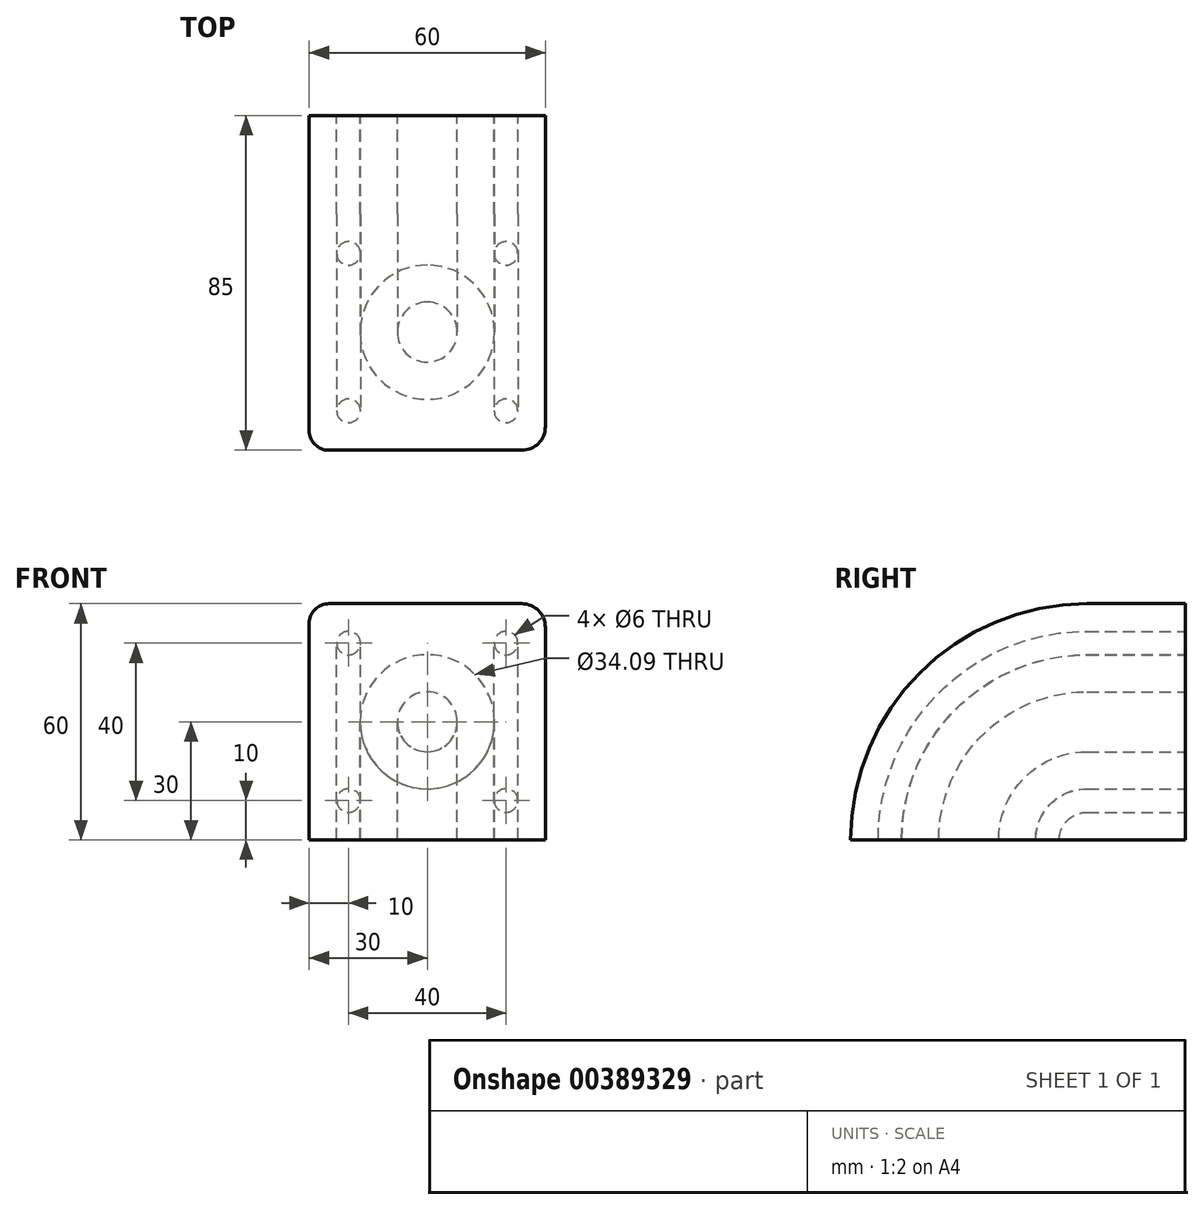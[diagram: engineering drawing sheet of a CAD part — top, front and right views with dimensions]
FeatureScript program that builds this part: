
annotation { "Feature Type Name" : "Feature", "Feature Type Description" : "" }
export const myFeature = defineFeature(function(context is Context, id is Id, definition is map)
    precondition{}
    {
        {
            var Q0;
            Q0=qCreatedBy(makeId("Front.planeOp"),FACE);
            var sketch = newSketch(context, id + "F0", { "sketchPlane" : qUnion([Q0])});
            skLineSegment(sketch, "E0.bottom", {"start": v(-30, 30) * mm, "end": v(24, 30) * mm});
            skLineSegment(sketch, "E0.top", {"start": v(-30, -30) * mm, "end": v(30, -30) * mm});
            skLineSegment(sketch, "E0.left", {"start": v(-30, 30) * mm, "end": v(-30, -30) * mm});
            skLineSegment(sketch, "E0.right", {"start": v(30, 24) * mm, "end": v(30, -30) * mm});
            skCircle(sketch, "E1", {"center": v(-20, 20) * mm, "radius": 3 * mm});
            skCircle(sketch, "E2", {"center": v(20, 20) * mm, "radius": 3 * mm});
            skCircle(sketch, "E3", {"center": v(20, -20) * mm, "radius": 3 * mm});
            skCircle(sketch, "E4", {"center": v(-20, -20) * mm, "radius": 3 * mm});
            skLineSegment(sketch, "E5.bottom", {"start": v(-20, 20) * mm, "end": v(20, 20) * mm, "construction": true});
            skLineSegment(sketch, "E5.top", {"start": v(-20, -20) * mm, "end": v(20, -20) * mm, "construction": true});
            skLineSegment(sketch, "E5.left", {"start": v(-20, 20) * mm, "end": v(-20, -20) * mm, "construction": true});
            skLineSegment(sketch, "E5.right", {"start": v(20, 20) * mm, "end": v(20, -20) * mm, "construction": true});
            skLineSegment(sketch, "E6", {"start": v(-20, 20) * mm, "end": v(20, -20) * mm, "construction": true});
            skLineSegment(sketch, "E7", {"start": v(30, 30) * mm, "end": v(-30, -30) * mm, "construction": true});
            skPoint(sketch, "E8.visualSharp", {"position": v(-30, 30) * mm});
            skPoint(sketch, "E9.visualSharp", {"position": v(30, 30) * mm});
            skArc(sketch, "E9.filletArc", {"start": v(30, 24) * mm, "mid": v(28.24, 28.24) * mm, "end": v(24, 30) * mm});
            skCircle(sketch, "E10", {"center": v(0, 0) * mm, "radius": 17.05 * mm});
            skCircle(sketch, "E11", {"center": v(0, 0) * mm, "radius": 7.61 * mm});
            skSolve(sketch);
        }
        {
            var Q0;
            Q0 = qSketchRegion(id + "F0", true);
            var Q1;
            Q1=makeQuery(id+"F0.imprint","IMPRINT",FACE,{"disambiguationData":[TD([[makeQuery(id+"F0.imprint","IMPRINT",EDGE,{"derivedFrom":sQuery(id+"F0.wireOp",EDGE,"E11")}),1.0]])]});
            extrude(context, id + "F1", {"entities" : qUnion([Q0, Q1]), "depth" : 25 * mm, "offsetDistance" : 25 * mm});
        }
        {
            var Q0;
            Q0=makeQuery(id+"F1.opExtrude","CAP_FACE",FACE,{"disambiguationData":[OSD([sQuery(id+"F0.wireOp",EDGE,"E0.bottom"),sQuery(id+"F0.wireOp",EDGE,"E0.top"),sQuery(id+"F0.wireOp",EDGE,"E0.left"),sQuery(id+"F0.wireOp",EDGE,"E0.right"),sQuery(id+"F0.wireOp",EDGE,"E1"),sQuery(id+"F0.wireOp",EDGE,"E2"),sQuery(id+"F0.wireOp",EDGE,"E3"),sQuery(id+"F0.wireOp",EDGE,"E4")])],"isStart":false});
            var Q1;
            Q1=makeQuery(id+"F1.opExtrude","CAP_FACE",FACE,{"disambiguationData":[OSD([sQuery(id+"F0.wireOp",EDGE,"E11")])],"isStart":false});
            var Q2;
            Q2=makeQuery(id+"F1.opExtrude","CAP_EDGE",EDGE,{"disambiguationData":[OSD([sQuery(id+"F0.wireOp",EDGE,"E0.top")])],"isStart":false});
            revolve(context, id + "F2", {"operationType" : NewBodyOperationType.ADD, "surfaceOperationType" : NewSurfaceOperationType.NEW, "entities" : qUnion([Q0, Q1]), "axis" : qUnion([Q2]), "revolveType" : RevolveType.ONE_DIRECTION, "angle" : 90 * degree});
        }
        {
            var Q0;
            Q0=makeQuery(id+"F2.opRevolve","SWEPT_EDGE",EDGE,{"disambiguationData":[OSD([sQuery(id+"F0.wireOp",EDGE,"E0.bottom"),sQuery(id+"F0.wireOp",EDGE,"E0.left")])]});
            var Q1;
            Q1=makeQuery(id+"F1.opExtrude","SWEPT_EDGE",EDGE,{"disambiguationData":[OSD([sQuery(id+"F0.wireOp",EDGE,"E0.bottom"),sQuery(id+"F0.wireOp",EDGE,"E0.left")])]});
            fillet(context, id + "F3", {"entities" : qUnion([Q0, Q1]), "radius" : 5 * mm, "tangentPropagation" : true, "allowEdgeOverflow" : false});
        }
    });
